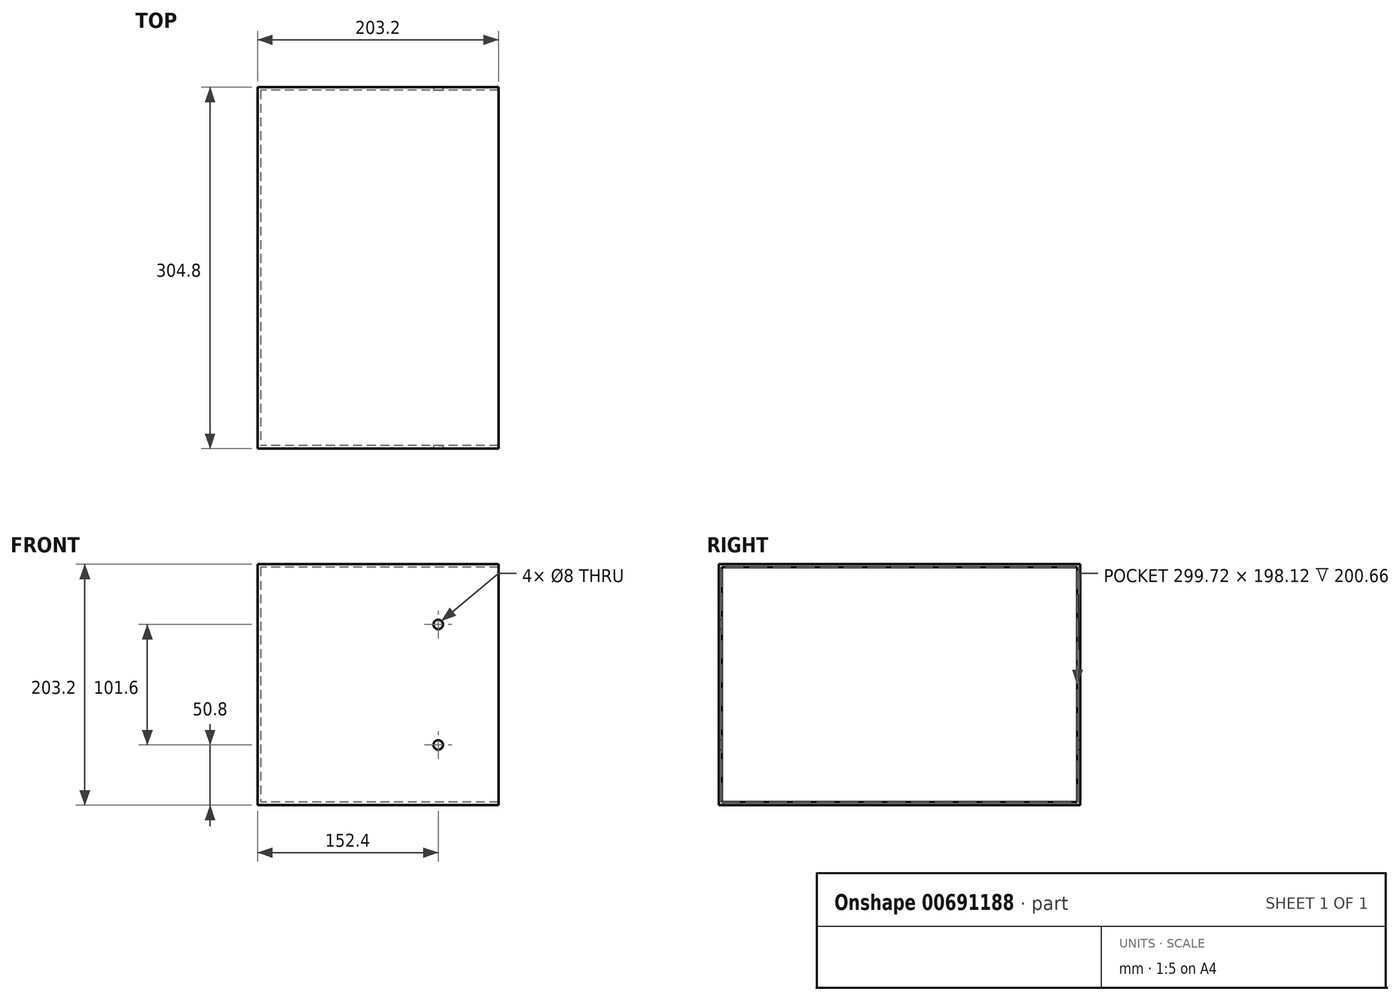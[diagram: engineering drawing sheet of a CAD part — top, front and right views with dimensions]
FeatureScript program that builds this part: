
annotation { "Feature Type Name" : "Feature", "Feature Type Description" : "" }
export const myFeature = defineFeature(function(context is Context, id is Id, definition is map)
    precondition{}
    {
        {
            var Q0;
            Q0=qCreatedBy(makeId("Right.planeOp"),FACE);
            var sketch = newSketch(context, id + "F0", { "sketchPlane" : qUnion([Q0])});
            skLineSegment(sketch, "E0", {"start": v(0, 0) * mm, "end": v(0, -203.2) * mm});
            skLineSegment(sketch, "E1", {"start": v(0, -203.2) * mm, "end": v(304.8, -203.2) * mm});
            skLineSegment(sketch, "E2", {"start": v(304.8, -203.2) * mm, "end": v(304.8, 0) * mm});
            skLineSegment(sketch, "E3", {"start": v(304.8, 0) * mm, "end": v(0, 0) * mm});
            skSolve(sketch);
        }
        {
            var Q0;
            Q0 = qSketchRegion(id + "F0", true);
            extrude(context, id + "F1", {"entities" : qUnion([Q0]), "depth" : 203.2 * mm, "offsetDistance" : 25.4 * mm});
        }
        {
            var Q0;
            Q0=makeQuery(id+"F1.opExtrude","CAP_FACE",FACE,{"disambiguationData":[OSD([sQuery(id+"F0.wireOp",EDGE,"E0"),sQuery(id+"F0.wireOp",EDGE,"E1"),sQuery(id+"F0.wireOp",EDGE,"E2"),sQuery(id+"F0.wireOp",EDGE,"E3")])],"isStart":false});
            shell(context, id + "F2", {"entities" : qUnion([Q0]), "thickness" : 2.54 * mm});
        }
        {
            var Q0;
            Q0=makeQuery(id+"F1.opExtrude","SWEPT_FACE",FACE,{"disambiguationData":[OSD([sQuery(id+"F0.wireOp",EDGE,"E0")])]});
            var sketch = newSketch(context, id + "F3", { "sketchPlane" : qUnion([Q0])});
            skLineSegment(sketch, "E4", {"start": v(0, 0) * mm, "end": v(152.4, 0) * mm});
            skLineSegment(sketch, "E5", {"start": v(152.4, 0) * mm, "end": v(152.4, -50.8) * mm});
            skLineSegment(sketch, "E6", {"start": v(152.4, -50.8) * mm, "end": v(152.4, -152.4) * mm});
            skSolve(sketch);
        }
        {
            var Q0;
            Q0=sQuery(id+"F3.wireOp",VERTEX,"E6.start");
            var Q1;
            Q1=sQuery(id+"F3.wireOp",VERTEX,"E6.end");
            var Q2;
            Q2=makeQuery(id+"F1.opExtrude","SWEPT_BODY",BODY,{"disambiguationData":[OSD([sQuery(id+"F0.wireOp",EDGE,"E0"),sQuery(id+"F0.wireOp",EDGE,"E1"),sQuery(id+"F0.wireOp",EDGE,"E2"),sQuery(id+"F0.wireOp",EDGE,"E3")])]});
            hole(context, id + "F4", {"style" : HoleStyle.SIMPLE, "endStyle" : HoleEndStyle.THROUGH, "holeDiameter" : 8 * mm, "majorDiameter" : 6.35 * mm, "isTappedThrough" : true, "tappedDepth" : 12.7 * mm, "tapClearance" : 3, "locations" : qUnion([Q0, Q1]), "scope" : qUnion([Q2])});
        }
    });
